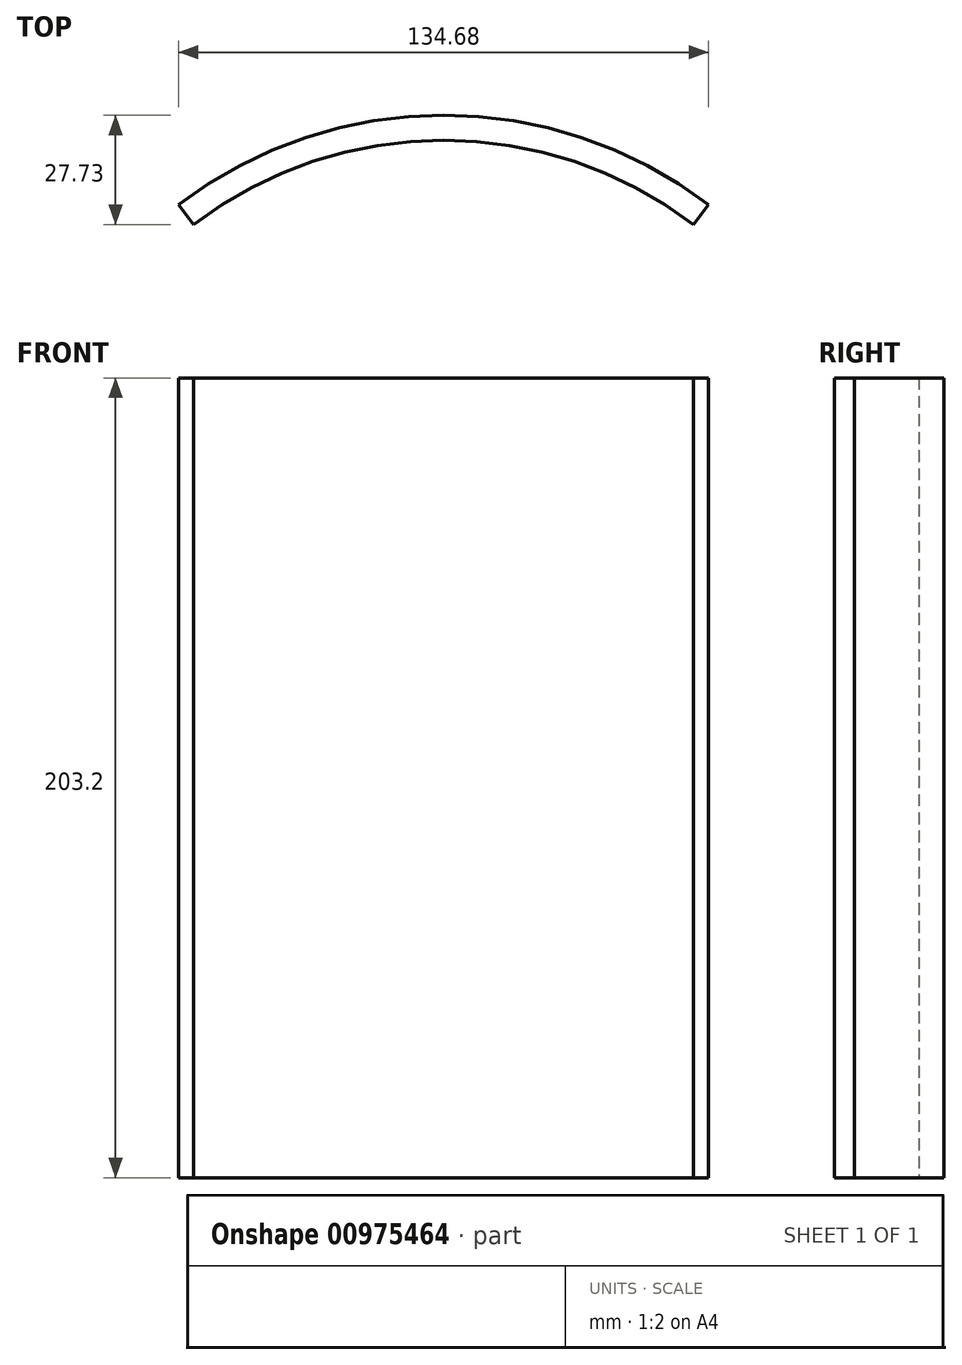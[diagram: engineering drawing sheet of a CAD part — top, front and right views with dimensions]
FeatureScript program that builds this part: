
annotation { "Feature Type Name" : "Feature", "Feature Type Description" : "" }
export const myFeature = defineFeature(function(context is Context, id is Id, definition is map)
    precondition{}
    {
        {
            var Q0;
            Q0=qCreatedBy(makeId("Top.planeOp"),FACE);
            var sketch = newSketch(context, id + "F0", { "sketchPlane" : qUnion([Q0])});
            skArc(sketch, "E0", {"start": v(63.5, 0) * mm, "mid": v(0, 21.38) * mm, "end": v(-63.5, 0) * mm});
            skArc(sketch, "E1.0", {"start": v(67.34, 5.06) * mm, "mid": v(0, 27.73) * mm, "end": v(-67.34, 5.06) * mm});
            skLineSegment(sketch, "E2", {"start": v(-67.34, 5.06) * mm, "end": v(-63.5, 0) * mm});
            skLineSegment(sketch, "E3", {"start": v(63.5, 0) * mm, "end": v(67.34, 5.06) * mm});
            skSolve(sketch);
        }
        {
            var Q0;
            Q0=makeQuery(id+"F0.imprint","IMPRINT",FACE,{"disambiguationData":[TD([[makeQuery(id+"F0.imprint","IMPRINT",EDGE,{"derivedFrom":sQuery(id+"F0.wireOp",EDGE,"E0")}),-1.0]])]});
            extrude(context, id + "F1", {"entities" : qUnion([Q0]), "depth" : 203.2 * mm, "offsetDistance" : 25.4 * mm});
        }
    });
